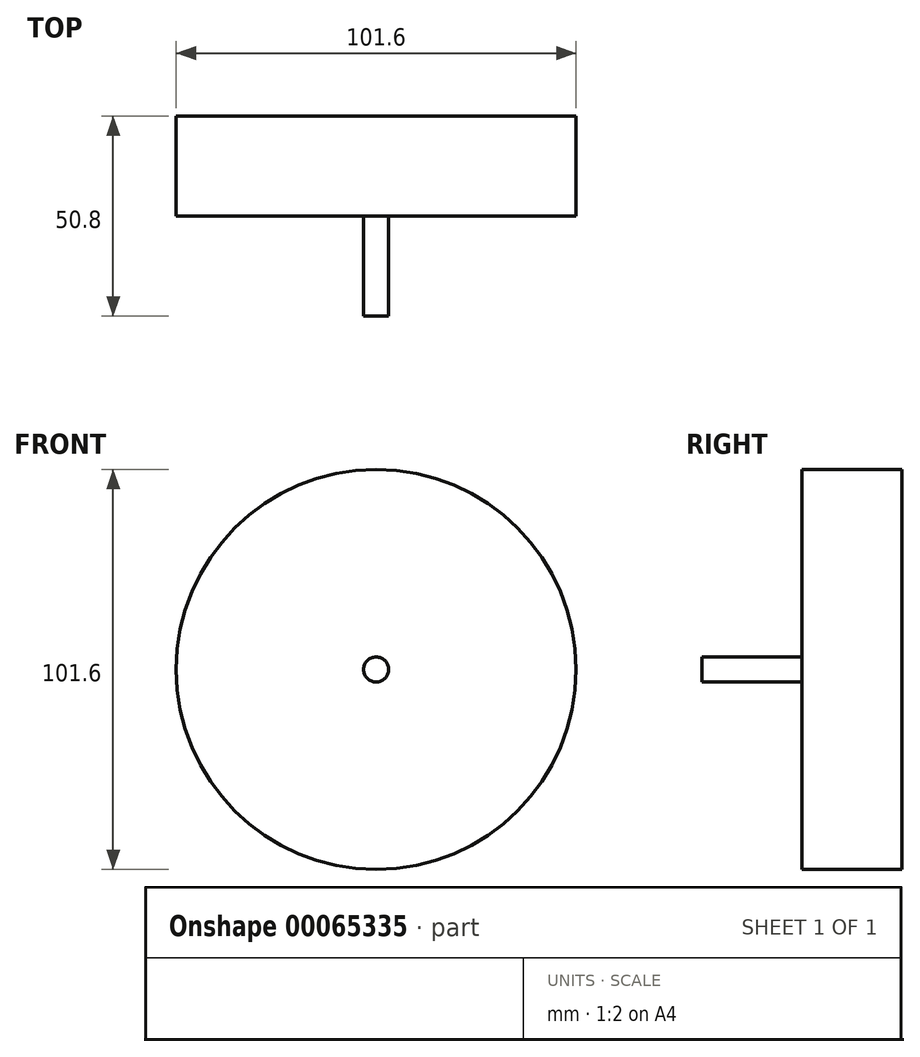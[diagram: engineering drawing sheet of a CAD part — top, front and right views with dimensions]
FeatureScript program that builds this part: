
annotation { "Feature Type Name" : "Feature", "Feature Type Description" : "" }
export const myFeature = defineFeature(function(context is Context, id is Id, definition is map)
    precondition{}
    {
        {
            var Q0;
            Q0=qCreatedBy(makeId("Front.planeOp"),FACE);
            var sketch = newSketch(context, id + "F0", { "sketchPlane" : qUnion([Q0])});
            skCircle(sketch, "E0", {"center": v(0, 0) * mm, "radius": 50.8 * mm});
            skSolve(sketch);
        }
        {
            var Q0;
            Q0=makeQuery(id+"F0.imprint","IMPRINT",FACE,{"disambiguationData":[TD([[makeQuery(id+"F0.imprint","IMPRINT",EDGE,{"derivedFrom":sQuery(id+"F0.wireOp",EDGE,"E0")}),1.0]])]});
            var sketch = newSketch(context, id + "F1", { "sketchPlane" : qUnion([Q0])});
            skCircle(sketch, "E1", {"center": v(0, 0) * mm, "radius": 3.18 * mm});
            skSolve(sketch);
        }
        {
            var Q0;
            Q0 = qSketchRegion(id + "F0", true);
            extrude(context, id + "F2", {"entities" : qUnion([Q0]), "depth" : 25.4 * mm});
        }
        {
            var Q0;
            Q0 = qSketchRegion(id + "F1", true);
            extrude(context, id + "F3", {"entities" : qUnion([Q0]), "operationType" : NewBodyOperationType.ADD, "depth" : 50.8 * mm});
        }
    });
